# Revit family: SpecEquip_BoilingUnit_Zip UK_On-Wall_HydroBoilPlus
name_source: partatom
category: Specialty Equipment
revit_build: Autodesk Revit 2016 (Build: 20190508_0715(x64)
units: mm (PartAtom-declared; Revit-internal decimal feet)

## family parameters
Always vertical = Yes
Cut with Voids When Loaded = Yes
OmniClass Number = 23.75.70.17.21
OmniClass Title = Embedded Water Heating Terminals
Part Type = Normal
Room Calculation Point = No
Round Connector Dimension = Use Diameter
Shared = No
Work Plane-Based = No

## types (3) — shared parameters
Body Material = z_Zip_White
Description = HydroBoil Plus - On wall boiling water
IfcExportAs = IfcBoiler
IfcExportType = WATER
Manufacturer = ZIP Water UK
Manufacturer_URL__Product Specific = https://specify.zipwater.co.uk
ModifiedIssue_ANZRS = 20190830 $
Tap Material = z_Zip_Red
URL = https://www.zipwater.co.uk
Uniclass2015Code = Pr_60_60_96_28
Uniclass2015Title = Electric storage water heaters
Uniclass2015Version = Products v1.14

## per-type parameters (varying)
| type | Manufacturer_Overall Depth | Manufacturer_Overall Height | Manufacturer_Overall Width | Manufacturer_Spec Code | Model | Type Comments |
| 7.5l | 198 mm  [stored 0.649606 ft] | 578 mm  [stored 1.89633 ft] | 318 mm  [stored 1.04331 ft] | 307562 | 307562 | 7.5 Litre Hydroboil Plus |
| 5.0l | 198 mm  [stored 0.649606 ft] | 465 mm | 318 mm  [stored 1.04331 ft] | 305562 | 305562 | 5.0 Litre Hydroboil Plus |
| 3.0l | 180 mm | 431 mm | 289 mm | 303562 | 303562 | 3.0 Litre Hydroboil Plus |

note: [stored X ft] marks values corroborated as IEEE doubles in the binary element streams (Revit-internal decimal feet)

## geometry (parser evidence)
native form markers: Sweep x3
no freeform markers — native parametric forms only
